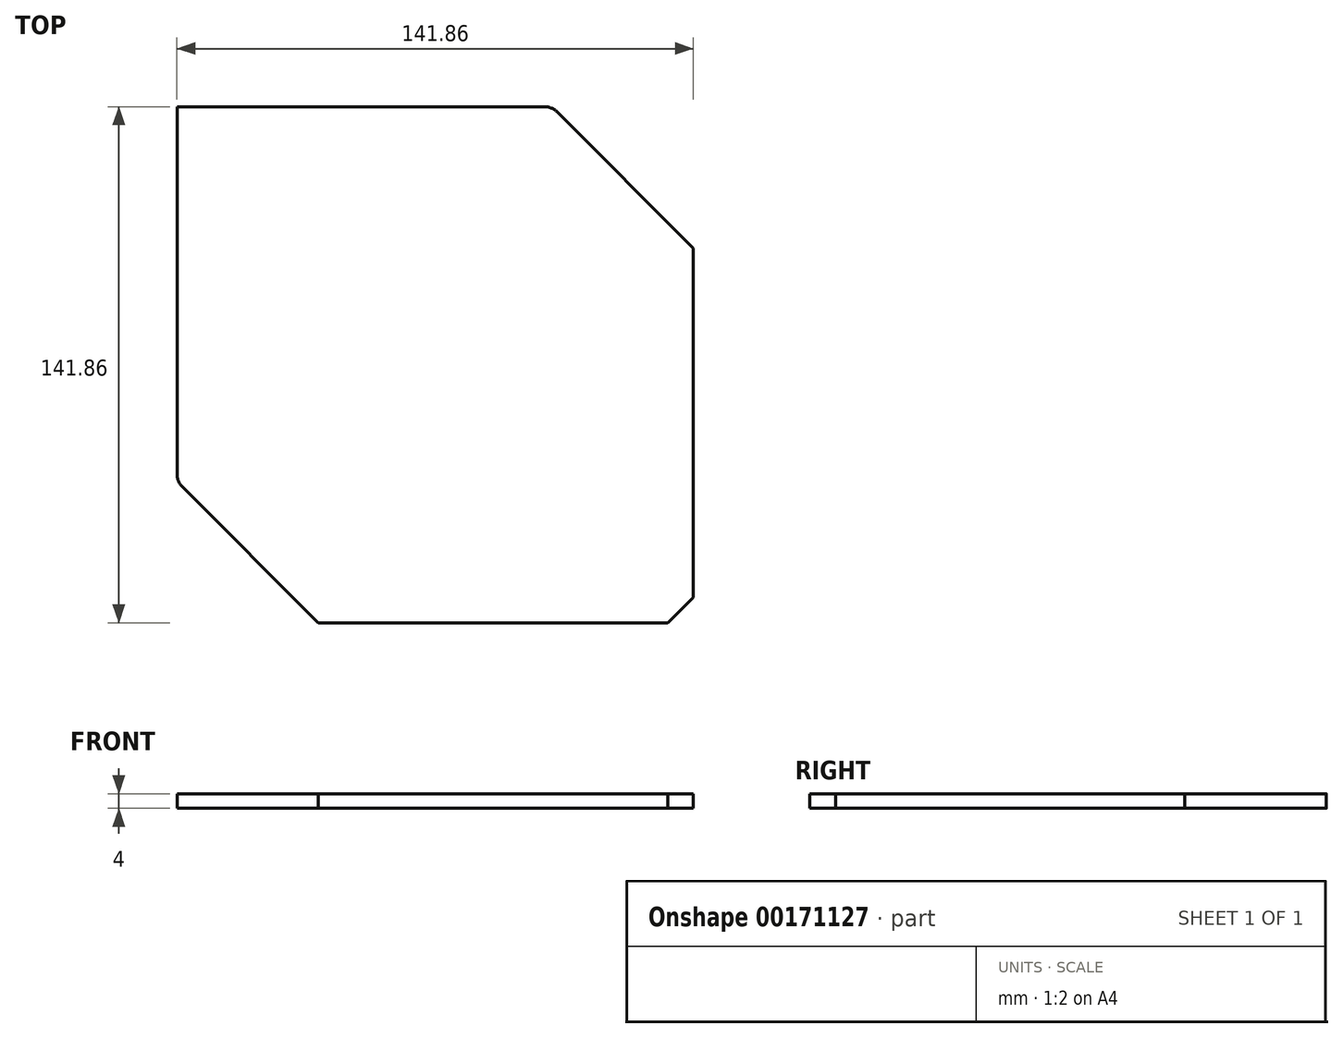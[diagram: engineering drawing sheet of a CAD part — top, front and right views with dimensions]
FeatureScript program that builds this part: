
annotation { "Feature Type Name" : "Feature", "Feature Type Description" : "" }
export const myFeature = defineFeature(function(context is Context, id is Id, definition is map)
    precondition{}
    {
        {
            var Q0;
            Q0=qCreatedBy(makeId("Top.planeOp"),FACE);
            var sketch = newSketch(context, id + "F0", { "sketchPlane" : qUnion([Q0])});
            skLineSegment(sketch, "E0.bottom", {"start": v(55, 55) * mm, "end": v(-55, 55) * mm});
            skLineSegment(sketch, "E0.top", {"start": v(55, -55) * mm, "end": v(-55, -55) * mm});
            skLineSegment(sketch, "E0.left", {"start": v(55, 55) * mm, "end": v(55, -55) * mm});
            skLineSegment(sketch, "E0.right", {"start": v(-55, 55) * mm, "end": v(-55, -55) * mm});
            skPoint(sketch, "E0.middle", {"position": v(0, 0) * mm});
            skSolve(sketch);
        }
        {
            var Q0;
            Q0=qSketchRegion(id+"F0",true);
            extrude(context, id + "F1", {"entities" : qUnion([Q0]), "depth" : 5 * mm});
        }
        {
            var Q0;
            Q0=makeQuery(id+"F1.opExtrude","CAP_FACE",FACE,{"disambiguationData":[OSD([sQuery(id+"F0.wireOp",EDGE,"E0.bottom"),sQuery(id+"F0.wireOp",EDGE,"E0.top"),sQuery(id+"F0.wireOp",EDGE,"E0.left"),sQuery(id+"F0.wireOp",EDGE,"E0.right")])],"isStart":false});
            var sketch = newSketch(context, id + "F2", { "sketchPlane" : qUnion([Q0])});
            skLineSegment(sketch, "E1", {"start": v(-55, -55) * mm, "end": v(-55, -45) * mm});
            skLineSegment(sketch, "E2", {"start": v(-55, -45) * mm, "end": v(-50, -45) * mm});
            skLineSegment(sketch, "E3", {"start": v(-50, -45) * mm, "end": v(-50, -50) * mm});
            skLineSegment(sketch, "E4", {"start": v(-50, -50) * mm, "end": v(-45, -50) * mm});
            skLineSegment(sketch, "E5", {"start": v(-45, -50) * mm, "end": v(-45, -55) * mm});
            skLineSegment(sketch, "E6", {"start": v(-45, -55) * mm, "end": v(-55, -55) * mm});
            skLineSegment(sketch, "E7.MirrorCS", {"start": v(45, -55) * mm, "end": v(55, -55) * mm});
            skLineSegment(sketch, "E8.MirrorCS", {"start": v(45, -50) * mm, "end": v(45, -55) * mm});
            skLineSegment(sketch, "E9.MirrorCS", {"start": v(50, -50) * mm, "end": v(45, -50) * mm});
            skLineSegment(sketch, "E10.MirrorCS", {"start": v(50, -45) * mm, "end": v(50, -50) * mm});
            skLineSegment(sketch, "E11.MirrorCS", {"start": v(55, -55) * mm, "end": v(55, -45) * mm});
            skLineSegment(sketch, "E12.MirrorCS", {"start": v(55, -45) * mm, "end": v(50, -45) * mm});
            skLineSegment(sketch, "E13.MirrorCS", {"start": v(55, 45) * mm, "end": v(50, 45) * mm});
            skLineSegment(sketch, "E14.MirrorCS", {"start": v(-50, 45) * mm, "end": v(-50, 50) * mm});
            skLineSegment(sketch, "E15.MirrorCS", {"start": v(50, 50) * mm, "end": v(45, 50) * mm});
            skLineSegment(sketch, "E16.MirrorCS", {"start": v(50, 45) * mm, "end": v(50, 50) * mm});
            skLineSegment(sketch, "E17.MirrorCS", {"start": v(-50, 50) * mm, "end": v(-45, 50) * mm});
            skLineSegment(sketch, "E18.MirrorCS", {"start": v(-45, 50) * mm, "end": v(-45, 55) * mm});
            skLineSegment(sketch, "E19.MirrorCS", {"start": v(45, 50) * mm, "end": v(45, 55) * mm});
            skLineSegment(sketch, "E20.MirrorCS", {"start": v(-55, 45) * mm, "end": v(-50, 45) * mm});
            skLineSegment(sketch, "E21.MirrorCS", {"start": v(-45, 55) * mm, "end": v(-55, 55) * mm});
            skLineSegment(sketch, "E22.MirrorCS", {"start": v(55, 55) * mm, "end": v(55, 45) * mm});
            skLineSegment(sketch, "E23.MirrorCS", {"start": v(-55, 55) * mm, "end": v(-55, 45) * mm});
            skLineSegment(sketch, "E24.MirrorCS", {"start": v(45, 55) * mm, "end": v(55, 55) * mm});
            skSolve(sketch);
        }
        {
            var Q0;
            Q0=qSketchRegion(id+"F2",true);
            extrude(context, id + "F3", {"entities" : qUnion([Q0]), "operationType" : NewBodyOperationType.ADD, "depth" : 100 * mm});
        }
        {
            var Q0;
            Q0=makeQuery(id+"F3.boolean.opBoolean","MERGE",EDGE,{"derivedFrom":[makeQuery(id+"F1.opExtrude","SWEPT_EDGE",EDGE,{"disambiguationData":[OSD([sQuery(id+"F0.wireOp",EDGE,"E0.top"),sQuery(id+"F0.wireOp",EDGE,"E0.left")])]}),makeQuery(id+"F3.opExtrude","SWEPT_EDGE",EDGE,{"disambiguationData":[OSD([sQuery(id+"F2.wireOp",EDGE,"E7.MirrorCS"),sQuery(id+"F2.wireOp",EDGE,"E11.MirrorCS")])]})]});
            var Q1;
            Q1=makeQuery(id+"F3.boolean.opBoolean","MERGE",EDGE,{"derivedFrom":[makeQuery(id+"F1.opExtrude","SWEPT_EDGE",EDGE,{"disambiguationData":[OSD([sQuery(id+"F0.wireOp",EDGE,"E0.bottom"),sQuery(id+"F0.wireOp",EDGE,"E0.left")])]}),makeQuery(id+"F3.opExtrude","SWEPT_EDGE",EDGE,{"disambiguationData":[OSD([sQuery(id+"F2.wireOp",EDGE,"E22.MirrorCS"),sQuery(id+"F2.wireOp",EDGE,"E24.MirrorCS")])]})]});
            var Q2;
            Q2=makeQuery(id+"F3.boolean.opBoolean","MERGE",EDGE,{"derivedFrom":[makeQuery(id+"F1.opExtrude","SWEPT_EDGE",EDGE,{"disambiguationData":[OSD([sQuery(id+"F0.wireOp",EDGE,"E0.top"),sQuery(id+"F0.wireOp",EDGE,"E0.right")])]}),makeQuery(id+"F3.opExtrude","SWEPT_EDGE",EDGE,{"disambiguationData":[OSD([sQuery(id+"F2.wireOp",EDGE,"E6"),sQuery(id+"F2.wireOp",EDGE,"E1")])]})]});
            var Q3;
            Q3=makeQuery(id+"F3.boolean.opBoolean","MERGE",EDGE,{"derivedFrom":[makeQuery(id+"F1.opExtrude","SWEPT_EDGE",EDGE,{"disambiguationData":[OSD([sQuery(id+"F0.wireOp",EDGE,"E0.bottom"),sQuery(id+"F0.wireOp",EDGE,"E0.right")])]}),makeQuery(id+"F3.opExtrude","SWEPT_EDGE",EDGE,{"disambiguationData":[OSD([sQuery(id+"F2.wireOp",EDGE,"E23.MirrorCS"),sQuery(id+"F2.wireOp",EDGE,"E21.MirrorCS")])]})]});
            chamfer(context, id + "F4", {"entities" : qUnion([Q0, Q1, Q2, Q3]), "width" : 7 * mm, "tangentPropagation" : true});
        }
        {
            var Q0;
            Q0=makeQuery(id+"F1.opExtrude","CAP_FACE",FACE,{"disambiguationData":[OSD([sQuery(id+"F0.wireOp",EDGE,"E0.bottom"),sQuery(id+"F0.wireOp",EDGE,"E0.top"),sQuery(id+"F0.wireOp",EDGE,"E0.left"),sQuery(id+"F0.wireOp",EDGE,"E0.right")])],"isStart":true});
            var sketch = newSketch(context, id + "F5", { "sketchPlane" : qUnion([Q0])});
            skLineSegment(sketch, "E25", {"start": v(-55, 48) * mm, "end": v(-86.86, 16.14) * mm});
            skLineSegment(sketch, "E26", {"start": v(-86.86, 16.14) * mm, "end": v(-86.86, -86.86) * mm});
            skLineSegment(sketch, "E27.MirrorCS", {"start": v(16.14, -86.86) * mm, "end": v(-86.86, -86.86) * mm});
            skLineSegment(sketch, "E28.MirrorCS", {"start": v(48, -55) * mm, "end": v(16.14, -86.86) * mm});
            skSolve(sketch);
        }
        {
            var Q0;
            Q0=makeQuery(id+"F5.imprint","IMPRINT",FACE,{"disambiguationData":[TD([[makeQuery(id+"F5.imprint","IMPRINT",EDGE,{"derivedFrom":sQuery(id+"F5.wireOp",EDGE,"E25")}),1.0]])]});
            extrude(context, id + "F6", {"entities" : qUnion([Q0]), "operationType" : NewBodyOperationType.ADD, "oppositeDirection" : true, "depth" : 5 * mm});
        }
        {
            var Q0;
            {var subQ0=sQuery(id+"F0.wireOp",EDGE,"E0.right");var subQ1=sQuery(id+"F0.wireOp",EDGE,"E0.left");var subQ2=sQuery(id+"F0.wireOp",EDGE,"E0.top");var subQ3=sQuery(id+"F0.wireOp",EDGE,"E0.bottom");Q0=makeQuery(id+"F6.boolean.opBoolean","MERGE",FACE,{"derivedFrom":[makeQuery(id+"F1.opExtrude","CAP_FACE",FACE,{"disambiguationData":[OSD([subQ3,subQ2,subQ1,subQ0])],"isStart":false}),makeQuery(id+"F6.opExtrude","CAP_FACE",FACE,{"disambiguationData":[OSD([subQ3,subQ2,subQ1,subQ0,sQuery(id+"F2.wireOp",EDGE,"E23.MirrorCS"),sQuery(id+"F2.wireOp",EDGE,"E21.MirrorCS"),sQuery(id+"F5.wireOp",EDGE,"E25"),sQuery(id+"F5.wireOp",EDGE,"E26"),sQuery(id+"F5.wireOp",EDGE,"E27.MirrorCS"),sQuery(id+"F5.wireOp",EDGE,"E28.MirrorCS")])],"isStart":false})]});}
            var sketch = newSketch(context, id + "F7", { "sketchPlane" : qUnion([Q0])});
            skLineSegment(sketch, "E29", {"start": v(-55, -48) * mm, "end": v(-86.86, -16.14) * mm});
            skLineSegment(sketch, "E30", {"start": v(-86.86, -16.14) * mm, "end": v(-86.86, 86.86) * mm});
            skLineSegment(sketch, "E31", {"start": v(-50, 50) * mm, "end": v(-50.53, 49.47) * mm});
            skLineSegment(sketch, "E32", {"start": v(-50.53, 49.47) * mm, "end": v(-85.69, 84.63) * mm});
            skLineSegment(sketch, "E33", {"start": v(-85.69, -2.59) * mm, "end": v(-85.69, 84.63) * mm});
            skFitSpline(sketch, "E34", {"points": [v(-55, -45) * mm, v(-73.9, -25.88) * mm, v(-83.72, -11.72) * mm, v(-85.69, -2.27) * mm], "startDerivative": vector(-48.1, 46.47) * mm, "endDerivative": vector(-2.15, 37.07) * mm});
            skLineSegment(sketch, "E35.MirrorCS", {"start": v(-49.47, 50.53) * mm, "end": v(-84.63, 85.69) * mm});
            skLineSegment(sketch, "E36.MirrorCS", {"start": v(2.59, 85.69) * mm, "end": v(-84.63, 85.69) * mm});
            skLineSegment(sketch, "E37.MirrorCS", {"start": v(16.14, 86.86) * mm, "end": v(-86.86, 86.86) * mm});
            skLineSegment(sketch, "E38.MirrorCS", {"start": v(-50, 50) * mm, "end": v(-49.47, 50.53) * mm});
            skFitSpline(sketch, "E39.MirrorCS", {"points": [v(45, 55) * mm, v(25.88, 73.9) * mm, v(11.72, 83.72) * mm, v(2.27, 85.69) * mm], "startDerivative": vector(-46.47, 48.1) * mm, "endDerivative": vector(-37.07, 2.15) * mm});
            skLineSegment(sketch, "E40.MirrorCS", {"start": v(48, 55) * mm, "end": v(16.14, 86.86) * mm});
            skLineSegment(sketch, "E41", {"start": v(-55, -48) * mm, "end": v(-55, -45) * mm});
            skLineSegment(sketch, "E42", {"start": v(45, 55) * mm, "end": v(48, 55) * mm});
            skSolve(sketch);
        }
        {
            var Q0;
            Q0=makeQuery(id+"F7.imprint","IMPRINT",FACE,{"disambiguationData":[TD([[makeQuery(id+"F7.imprint","IMPRINT",EDGE,{"derivedFrom":sQuery(id+"F7.wireOp",EDGE,"E29")}),-1.0]])]});
            extrude(context, id + "F8", {"entities" : qUnion([Q0]), "operationType" : NewBodyOperationType.ADD, "depth" : 100 * mm});
        }
        {
            var Q0;
            Q0=makeQuery(id+"F8.opExtrude","SWEPT_EDGE",EDGE,{"disambiguationData":[OSD([sQuery(id+"F0.wireOp",EDGE,"E0.bottom"),sQuery(id+"F0.wireOp",EDGE,"E0.top"),sQuery(id+"F0.wireOp",EDGE,"E0.left"),sQuery(id+"F0.wireOp",EDGE,"E0.right"),sQuery(id+"F2.wireOp",EDGE,"E23.MirrorCS"),sQuery(id+"F2.wireOp",EDGE,"E21.MirrorCS"),sQuery(id+"F7.wireOp",EDGE,"E35.MirrorCS")])]});
            var Q1;
            Q1=makeQuery(id+"F8.opExtrude","SWEPT_EDGE",EDGE,{"disambiguationData":[OSD([sQuery(id+"F0.wireOp",EDGE,"E0.bottom"),sQuery(id+"F0.wireOp",EDGE,"E0.top"),sQuery(id+"F0.wireOp",EDGE,"E0.left"),sQuery(id+"F0.wireOp",EDGE,"E0.right"),sQuery(id+"F2.wireOp",EDGE,"E23.MirrorCS"),sQuery(id+"F2.wireOp",EDGE,"E21.MirrorCS"),sQuery(id+"F7.wireOp",EDGE,"E32")])]});
            fillet(context, id + "F9", {"entities" : qUnion([Q0, Q1]), "radius" : 3 * mm, "tangentPropagation" : true, "allowEdgeOverflow" : false});
        }
        {
            var Q0;
            {var subQ0=sQuery(id+"F2.wireOp",EDGE,"E19.MirrorCS");Q0=makeQuery(id+"F8.boolean.opBoolean","MERGE",EDGE,{"derivedFrom":[makeQuery(id+"F3.opExtrude","SWEPT_EDGE",EDGE,{"disambiguationData":[OSD([sQuery(id+"F0.wireOp",EDGE,"E0.bottom"),subQ0,sQuery(id+"F2.wireOp",EDGE,"E24.MirrorCS")])]}),makeQuery(id+"F8.opExtrude","SWEPT_EDGE",EDGE,{"disambiguationData":[OSD([subQ0,sQuery(id+"F7.wireOp",EDGE,"E39.MirrorCS"),sQuery(id+"F7.wireOp",EDGE,"E42")])]})]});}
            var Q1;
            {var subQ0=sQuery(id+"F2.wireOp",EDGE,"E2");Q1=makeQuery(id+"F8.boolean.opBoolean","MERGE",EDGE,{"derivedFrom":[makeQuery(id+"F3.opExtrude","SWEPT_EDGE",EDGE,{"disambiguationData":[OSD([sQuery(id+"F0.wireOp",EDGE,"E0.right"),subQ0,sQuery(id+"F2.wireOp",EDGE,"E1")])]}),makeQuery(id+"F8.opExtrude","SWEPT_EDGE",EDGE,{"disambiguationData":[OSD([subQ0,sQuery(id+"F7.wireOp",EDGE,"E34"),sQuery(id+"F7.wireOp",EDGE,"E41")])]})]});}
            var Q2;
            Q2=makeQuery(id+"F8.opExtrude","SWEPT_EDGE",EDGE,{"disambiguationData":[OSD([sQuery(id+"F7.wireOp",EDGE,"E32"),sQuery(id+"F7.wireOp",EDGE,"E33")])]});
            var Q3;
            Q3=makeQuery(id+"F8.opExtrude","SWEPT_EDGE",EDGE,{"disambiguationData":[OSD([sQuery(id+"F7.wireOp",EDGE,"E35.MirrorCS"),sQuery(id+"F7.wireOp",EDGE,"E36.MirrorCS")])]});
            fillet(context, id + "F10", {"entities" : qUnion([Q0, Q1, Q2, Q3]), "radius" : 3 * mm, "tangentPropagation" : true, "allowEdgeOverflow" : false});
        }
        {
            var Q0;
            Q0=makeQuery(id+"F8.boolean.opBoolean","MERGE",EDGE,{"derivedFrom":[makeQuery(id+"F6.opExtrude","SWEPT_EDGE",EDGE,{"disambiguationData":[OSD([sQuery(id+"F5.wireOp",EDGE,"E25"),sQuery(id+"F5.wireOp",EDGE,"E26")])]}),makeQuery(id+"F8.opExtrude","SWEPT_EDGE",EDGE,{"disambiguationData":[OSD([sQuery(id+"F7.wireOp",EDGE,"E29"),sQuery(id+"F7.wireOp",EDGE,"E30")])]})]});
            var Q1;
            Q1=makeQuery(id+"F8.boolean.opBoolean","MERGE",EDGE,{"derivedFrom":[makeQuery(id+"F6.opExtrude","SWEPT_EDGE",EDGE,{"disambiguationData":[OSD([sQuery(id+"F5.wireOp",EDGE,"E27.MirrorCS"),sQuery(id+"F5.wireOp",EDGE,"E28.MirrorCS")])]}),makeQuery(id+"F8.opExtrude","SWEPT_EDGE",EDGE,{"disambiguationData":[OSD([sQuery(id+"F7.wireOp",EDGE,"E37.MirrorCS"),sQuery(id+"F7.wireOp",EDGE,"E40.MirrorCS")])]})]});
            fillet(context, id + "F11", {"entities" : qUnion([Q0, Q1]), "radius" : 5 * mm, "tangentPropagation" : true, "allowEdgeOverflow" : false});
        }
        {
            var Q0;
            Q0=makeQuery(id+"F8.boolean.opBoolean","MERGE",FACE,{"derivedFrom":[makeQuery(id+"F6.opExtrude","SWEPT_FACE",FACE,{"disambiguationData":[OSD([sQuery(id+"F5.wireOp",EDGE,"E27.MirrorCS")])]}),makeQuery(id+"F8.opExtrude","SWEPT_FACE",FACE,{"disambiguationData":[OSD([sQuery(id+"F7.wireOp",EDGE,"E37.MirrorCS")])]})]});
            var sketch = newSketch(context, id + "F12", { "sketchPlane" : qUnion([Q0])});
            skCircle(sketch, "E43", {"center": v(36.4, 52.5) * mm, "radius": 40 * mm});
            skSolve(sketch);
        }
        {
            var Q0;
            Q0=makeQuery(id+"F12.imprint","IMPRINT",FACE,{"disambiguationData":[TD([[makeQuery(id+"F12.imprint","IMPRINT",EDGE,{"derivedFrom":sQuery(id+"F12.wireOp",EDGE,"E43")}),1.0]])]});
            extrude(context, id + "F13", {"entities" : qUnion([Q0]), "operationType" : NewBodyOperationType.REMOVE, "oppositeDirection" : true, "depth" : 2 * mm});
        }
        {
            var Q0;
            Q0=makeQuery(id+"F8.boolean.opBoolean","MERGE",FACE,{"derivedFrom":[makeQuery(id+"F6.opExtrude","SWEPT_FACE",FACE,{"disambiguationData":[OSD([sQuery(id+"F5.wireOp",EDGE,"E26")])]}),makeQuery(id+"F8.opExtrude","SWEPT_FACE",FACE,{"disambiguationData":[OSD([sQuery(id+"F7.wireOp",EDGE,"E30")])]})]});
            var sketch = newSketch(context, id + "F14", { "sketchPlane" : qUnion([Q0])});
            skCircle(sketch, "E44", {"center": v(-36.4, 52.5) * mm, "radius": 40 * mm});
            skSolve(sketch);
        }
        {
            var Q0;
            Q0=qSketchRegion(id+"F14",true);
            extrude(context, id + "F15", {"entities" : qUnion([Q0]), "operationType" : NewBodyOperationType.REMOVE, "oppositeDirection" : true, "depth" : 2 * mm});
        }
        {
            var Q0;
            Q0=makeQuery(id+"F4.opChamfer","BLEND_FACE",FACE,{"disambiguationData":[OSD([sQuery(id+"F0.wireOp",EDGE,"E0.top"),sQuery(id+"F0.wireOp",EDGE,"E0.left"),sQuery(id+"F2.wireOp",EDGE,"E7.MirrorCS"),sQuery(id+"F2.wireOp",EDGE,"E11.MirrorCS")])]});
            var sketch = newSketch(context, id + "F16", { "sketchPlane" : qUnion([Q0])});
            skLineSegment(sketch, "E45", {"start": v(-74.5, 105) * mm, "end": v(-74.5, 4) * mm});
            skLineSegment(sketch, "E46", {"start": v(-74.5, 4) * mm, "end": v(75.34, 4) * mm});
            skLineSegment(sketch, "E47", {"start": v(75.34, 4) * mm, "end": v(75.34, 105) * mm});
            skLineSegment(sketch, "E48", {"start": v(0, 105) * mm, "end": v(4.95, 105) * mm});
            skLineSegment(sketch, "E49", {"start": v(-74.5, 105) * mm, "end": v(75.34, 105) * mm});
            skSolve(sketch);
        }
        {
            var Q0;
            Q0 = qSketchRegion(id + "F16", true);
            extrude(context, id + "F17", {"entities" : qUnion([Q0]), "operationType" : NewBodyOperationType.REMOVE, "oppositeDirection" : true, "depth" : 200 * mm});
        }
    });
